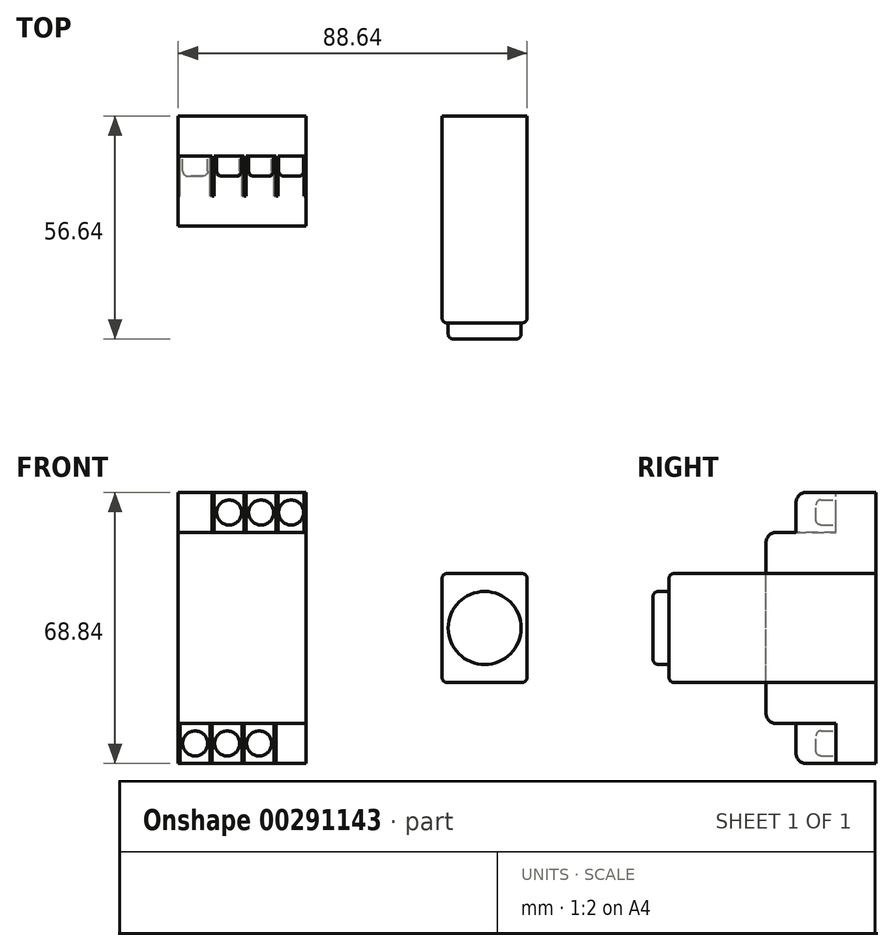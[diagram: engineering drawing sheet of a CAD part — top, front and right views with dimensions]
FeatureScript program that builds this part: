
annotation { "Feature Type Name" : "Feature", "Feature Type Description" : "" }
export const myFeature = defineFeature(function(context is Context, id is Id, definition is map)
    precondition{}
    {
        {
            var Q0;
            Q0=qCreatedBy(makeId("Front.planeOp"),FACE);
            var sketch = newSketch(context, id + "F0", { "sketchPlane" : qUnion([Q0])});
            skLineSegment(sketch, "E0.bottom", {"start": v(10.8, -13.84) * mm, "end": v(-10.8, -13.84) * mm});
            skLineSegment(sketch, "E0.top", {"start": v(10.8, 13.84) * mm, "end": v(-10.8, 13.84) * mm});
            skLineSegment(sketch, "E0.left", {"start": v(10.8, -13.84) * mm, "end": v(10.8, 13.84) * mm});
            skLineSegment(sketch, "E0.right", {"start": v(-10.8, -13.84) * mm, "end": v(-10.8, 13.84) * mm});
            skPoint(sketch, "E0.middle", {"position": v(0, 0) * mm});
            skSolve(sketch);
        }
        {
            var Q0;
            Q0 = qSketchRegion(id + "F0", true);
            extrude(context, id + "F1", {"entities" : qUnion([Q0]), "depth" : 52.58 * mm});
        }
        {
            var Q0;
            Q0=makeQuery(id+"F1.opExtrude","CAP_FACE",FACE,{"disambiguationData":[OSD([sQuery(id+"F0.wireOp",EDGE,"E0.bottom"),sQuery(id+"F0.wireOp",EDGE,"E0.top"),sQuery(id+"F0.wireOp",EDGE,"E0.left"),sQuery(id+"F0.wireOp",EDGE,"E0.right")])],"isStart":false});
            var sketch = newSketch(context, id + "F2", { "sketchPlane" : qUnion([Q0])});
            skCircle(sketch, "E1", {"center": v(0, 0) * mm, "radius": 9.27 * mm});
            skSolve(sketch);
        }
        {
            var Q0;
            Q0 = qSketchRegion(id + "F2", true);
            extrude(context, id + "F3", {"entities" : qUnion([Q0]), "operationType" : NewBodyOperationType.ADD, "depth" : 4.06 * mm});
        }
        {
            var Q0;
            Q0=makeQuery(id+"F3.opExtrude","CAP_EDGE",EDGE,{"disambiguationData":[OSD([sQuery(id+"F2.wireOp",EDGE,"E1")])],"isStart":false});
            fillet(context, id + "F4", {"entities" : qUnion([Q0]), "radius" : 1.27 * mm, "tangentPropagation" : true, "allowEdgeOverflow" : false});
        }
        {
            var Q0;
            Q0=makeQuery(id+"F1.opExtrude","CAP_EDGE",EDGE,{"disambiguationData":[OSD([sQuery(id+"F0.wireOp",EDGE,"E0.left")])],"isStart":false});
            var Q1;
            Q1=makeQuery(id+"F1.opExtrude","CAP_EDGE",EDGE,{"disambiguationData":[OSD([sQuery(id+"F0.wireOp",EDGE,"E0.bottom")])],"isStart":false});
            var Q2;
            Q2=makeQuery(id+"F1.opExtrude","CAP_EDGE",EDGE,{"disambiguationData":[OSD([sQuery(id+"F0.wireOp",EDGE,"E0.top")])],"isStart":false});
            var Q3;
            Q3=makeQuery(id+"F1.opExtrude","CAP_EDGE",EDGE,{"disambiguationData":[OSD([sQuery(id+"F0.wireOp",EDGE,"E0.right")])],"isStart":false});
            var Q4;
            Q4=makeQuery(id+"F1.opExtrude","SWEPT_EDGE",EDGE,{"disambiguationData":[OSD([sQuery(id+"F0.wireOp",EDGE,"E0.top"),sQuery(id+"F0.wireOp",EDGE,"E0.left")])]});
            var Q5;
            Q5=makeQuery(id+"F1.opExtrude","SWEPT_EDGE",EDGE,{"disambiguationData":[OSD([sQuery(id+"F0.wireOp",EDGE,"E0.bottom"),sQuery(id+"F0.wireOp",EDGE,"E0.left")])]});
            var Q6;
            Q6=makeQuery(id+"F1.opExtrude","SWEPT_EDGE",EDGE,{"disambiguationData":[OSD([sQuery(id+"F0.wireOp",EDGE,"E0.top"),sQuery(id+"F0.wireOp",EDGE,"E0.right")])]});
            var Q7;
            Q7=makeQuery(id+"F1.opExtrude","SWEPT_EDGE",EDGE,{"disambiguationData":[OSD([sQuery(id+"F0.wireOp",EDGE,"E0.bottom"),sQuery(id+"F0.wireOp",EDGE,"E0.right")])]});
            fillet(context, id + "F5", {"entities" : qUnion([Q0, Q1, Q2, Q3, Q4, Q5, Q6, Q7]), "radius" : 1.27 * mm, "tangentPropagation" : true, "allowEdgeOverflow" : false});
        }
        {
            var Q0;
            Q0=qCreatedBy(makeId("Front.planeOp"),FACE);
            var sketch = newSketch(context, id + "F6", { "sketchPlane" : qUnion([Q0])});
            skLineSegment(sketch, "E2.bottom", {"start": v(-77.85, -34.42) * mm, "end": v(-45.34, -34.42) * mm});
            skLineSegment(sketch, "E2.top", {"start": v(-77.85, 34.42) * mm, "end": v(-45.34, 34.42) * mm});
            skLineSegment(sketch, "E2.left", {"start": v(-77.85, -34.42) * mm, "end": v(-77.85, 34.42) * mm});
            skLineSegment(sketch, "E2.right", {"start": v(-45.34, -34.42) * mm, "end": v(-45.34, 34.42) * mm});
            skPoint(sketch, "E2.middle", {"position": v(-61.6, 0) * mm});
            skLineSegment(sketch, "E3.bottom", {"start": v(-77.85, 24.26) * mm, "end": v(-45.34, 24.26) * mm});
            skLineSegment(sketch, "E3.top", {"start": v(-77.85, -24.26) * mm, "end": v(-45.34, -24.26) * mm});
            skLineSegment(sketch, "E3.left", {"start": v(-77.85, 24.26) * mm, "end": v(-77.85, -24.26) * mm});
            skLineSegment(sketch, "E3.right", {"start": v(-45.34, 24.26) * mm, "end": v(-45.34, -24.26) * mm});
            skSolve(sketch);
        }
        {
            var Q0;
            Q0=makeQuery(id+"F6.imprint","IMPRINT",FACE,{"disambiguationData":[TD([[makeQuery(id+"F6.imprint","IMPRINT",EDGE,{"derivedFrom":sQuery(id+"F6.wireOp",EDGE,"E3.bottom")}),-1.0]])]});
            extrude(context, id + "F7", {"entities" : qUnion([Q0]), "depth" : 27.94 * mm});
        }
        {
            var Q0;
            {var subQ0=sQuery(id+"F6.wireOp",EDGE,"E2.top");Q0=makeQuery(id+"F6.imprint","IMPRINT",FACE,{"disambiguationData":[TD([[makeQuery(id+"F6.imprint","IMPRINT",EDGE,{"derivedFrom":subQ0}),-1.0]])]});}
            var Q1;
            {var subQ0=sQuery(id+"F6.wireOp",EDGE,"E2.bottom");Q1=makeQuery(id+"F6.imprint","IMPRINT",FACE,{"disambiguationData":[TD([[makeQuery(id+"F6.imprint","IMPRINT",EDGE,{"derivedFrom":subQ0}),1.0]])]});}
            extrude(context, id + "F8", {"entities" : qUnion([Q0, Q1]), "operationType" : NewBodyOperationType.ADD, "depth" : 10.16 * mm});
        }
        {
            var Q0;
            Q0=makeQuery(id+"F8.opExtrude","CAP_FACE",FACE,{"disambiguationData":[OSD([sQuery(id+"F6.wireOp",EDGE,"E2.top"),sQuery(id+"F6.wireOp",EDGE,"E2.left"),sQuery(id+"F6.wireOp",EDGE,"E2.right"),sQuery(id+"F6.wireOp",EDGE,"E3.bottom")])],"isStart":false});
            var sketch = newSketch(context, id + "F9", { "sketchPlane" : qUnion([Q0])});
            skLineSegment(sketch, "E4.bottom", {"start": v(-45.34, 34.42) * mm, "end": v(-69.22, 34.42) * mm});
            skLineSegment(sketch, "E4.top", {"start": v(-45.34, 24.26) * mm, "end": v(-69.22, 24.26) * mm});
            skLineSegment(sketch, "E4.left", {"start": v(-45.34, 34.42) * mm, "end": v(-45.34, 24.26) * mm});
            skLineSegment(sketch, "E4.right", {"start": v(-69.22, 34.42) * mm, "end": v(-69.22, 24.26) * mm});
            skSolve(sketch);
        }
        {
            var Q0;
            Q0 = qSketchRegion(id + "F9", true);
            extrude(context, id + "F10", {"entities" : qUnion([Q0]), "operationType" : NewBodyOperationType.ADD, "depth" : 10.16 * mm});
        }
        {
            var Q0;
            Q0=makeQuery(id+"F10.opExtrude","CAP_EDGE",EDGE,{"disambiguationData":[OSD([sQuery(id+"F9.wireOp",EDGE,"E4.bottom")])],"isStart":false});
            fillet(context, id + "F11", {"entities" : qUnion([Q0]), "radius" : 2.54 * mm, "tangentPropagation" : true, "allowEdgeOverflow" : false});
        }
        {
            var Q0;
            Q0=makeQuery(id+"F10.opExtrude","CAP_FACE",FACE,{"disambiguationData":[OSD([sQuery(id+"F9.wireOp",EDGE,"E4.bottom"),sQuery(id+"F9.wireOp",EDGE,"E4.top"),sQuery(id+"F9.wireOp",EDGE,"E4.left"),sQuery(id+"F9.wireOp",EDGE,"E4.right")])],"isStart":false});
            var sketch = newSketch(context, id + "F12", { "sketchPlane" : qUnion([Q0])});
            skPoint(sketch, "E5.centerSnap0", {"position": v(-45.34, 28.07) * mm});
            skPoint(sketch, "E5.centerSnap1", {"position": v(-57.28, 31.88) * mm});
            skPoint(sketch, "E6.centerSnap0", {"position": v(-69.22, 28.07) * mm});
            skLineSegment(sketch, "E7", {"start": v(-68.7, 24.26) * mm, "end": v(-68.7, 34.42) * mm});
            skLineSegment(sketch, "E8", {"start": v(-69.22, 34.42) * mm, "end": v(-69.22, 24.26) * mm});
            skLineSegment(sketch, "E9", {"start": v(-69.22, 24.26) * mm, "end": v(-68.7, 24.26) * mm});
            skLineSegment(sketch, "E10", {"start": v(-61.09, 34.42) * mm, "end": v(-61.09, 24.26) * mm});
            skLineSegment(sketch, "E11", {"start": v(-69.22, 24.26) * mm, "end": v(-45.34, 24.26) * mm});
            skLineSegment(sketch, "E12", {"start": v(-45.34, 24.26) * mm, "end": v(-45.34, 34.42) * mm});
            skLineSegment(sketch, "E13", {"start": v(-69.22, 34.42) * mm, "end": v(-45.34, 34.42) * mm});
            skLineSegment(sketch, "E14", {"start": v(-60.58, 34.42) * mm, "end": v(-60.58, 24.26) * mm});
            skLineSegment(sketch, "E15", {"start": v(-52.96, 34.42) * mm, "end": v(-52.96, 24.26) * mm});
            skLineSegment(sketch, "E16", {"start": v(-52.45, 34.42) * mm, "end": v(-52.45, 24.26) * mm});
            skLineSegment(sketch, "E17", {"start": v(-45.85, 34.42) * mm, "end": v(-45.85, 24.26) * mm});
            skSolve(sketch);
        }
        {
            var Q0;
            {var subQ0=sQuery(id+"F12.wireOp",EDGE,"E16");var subQ1=sQuery(id+"F12.wireOp",EDGE,"E11");var subQ2=makeQuery(id+"F12.imprint","INTERSECT",VERTEX,{"derivedFrom":[subQ1,subQ0]});Q0=makeQuery(id+"F12.imprint","IMPRINT",FACE,{"disambiguationData":[TD([[makeQuery(id+"F12.imprint","IMPRINT",EDGE,{"disambiguationData":[TD([[subQ2,-1.0]])],"derivedFrom":subQ1}),1.0]])]});}
            var Q1;
            {var subQ0=sQuery(id+"F12.wireOp",EDGE,"E16");var subQ1=sQuery(id+"F12.wireOp",EDGE,"E13");var subQ2=makeQuery(id+"F12.imprint","INTERSECT",VERTEX,{"derivedFrom":[subQ1,subQ0]});Q1=makeQuery(id+"F12.imprint","IMPRINT",FACE,{"disambiguationData":[TD([[makeQuery(id+"F12.imprint","IMPRINT",EDGE,{"disambiguationData":[TD([[subQ2,-1.0]])],"derivedFrom":subQ1}),-1.0]])]});}
            var Q2;
            {var subQ0=sQuery(id+"F12.wireOp",EDGE,"E14");var subQ1=sQuery(id+"F12.wireOp",EDGE,"E11");var subQ2=makeQuery(id+"F12.imprint","INTERSECT",VERTEX,{"derivedFrom":[subQ1,subQ0]});Q2=makeQuery(id+"F12.imprint","IMPRINT",FACE,{"disambiguationData":[TD([[makeQuery(id+"F12.imprint","IMPRINT",EDGE,{"disambiguationData":[TD([[subQ2,-1.0]])],"derivedFrom":subQ1}),1.0]])]});}
            var Q3;
            {var subQ0=sQuery(id+"F12.wireOp",EDGE,"E14");var subQ1=sQuery(id+"F12.wireOp",EDGE,"E13");var subQ2=makeQuery(id+"F12.imprint","INTERSECT",VERTEX,{"derivedFrom":[subQ1,subQ0]});Q3=makeQuery(id+"F12.imprint","IMPRINT",FACE,{"disambiguationData":[TD([[makeQuery(id+"F12.imprint","IMPRINT",EDGE,{"disambiguationData":[TD([[subQ2,-1.0]])],"derivedFrom":subQ1}),-1.0]])]});}
            var Q4;
            {var subQ0=sQuery(id+"F12.wireOp",EDGE,"E11");var subQ1=sQuery(id+"F12.wireOp",EDGE,"E7");var subQ2=makeQuery(id+"F12.imprint","INTERSECT",VERTEX,{"derivedFrom":[subQ1,subQ0]});Q4=makeQuery(id+"F12.imprint","IMPRINT",FACE,{"disambiguationData":[TD([[makeQuery(id+"F12.imprint","IMPRINT",EDGE,{"disambiguationData":[TD([[subQ2,-1.0]])],"derivedFrom":subQ0}),1.0]])]});}
            var Q5;
            {var subQ0=sQuery(id+"F12.wireOp",EDGE,"E13");var subQ1=sQuery(id+"F12.wireOp",EDGE,"E7");var subQ2=makeQuery(id+"F12.imprint","INTERSECT",VERTEX,{"derivedFrom":[subQ1,subQ0]});Q5=makeQuery(id+"F12.imprint","IMPRINT",FACE,{"disambiguationData":[TD([[makeQuery(id+"F12.imprint","IMPRINT",EDGE,{"disambiguationData":[TD([[subQ2,-1.0]])],"derivedFrom":subQ0}),-1.0]])]});}
            extrude(context, id + "F13", {"entities" : qUnion([Q0, Q1, Q2, Q3, Q4, Q5]), "operationType" : NewBodyOperationType.REMOVE, "oppositeDirection" : true, "depth" : 10.16 * mm});
        }
        {
            var Q0;
            Q0=makeQuery(id+"F13.boolean.opBoolean","COPY",FACE,{"derivedFrom":makeQuery(id+"F13.opExtrude","CAP_FACE",FACE,{"disambiguationData":[OSD([sQuery(id+"F12.wireOp",EDGE,"E7"),sQuery(id+"F12.wireOp",EDGE,"E10"),sQuery(id+"F12.wireOp",EDGE,"E11"),sQuery(id+"F12.wireOp",EDGE,"E13")])],"isStart":false})});
            var sketch = newSketch(context, id + "F14", { "sketchPlane" : qUnion([Q0])});
            skCircle(sketch, "E18", {"center": v(-64.9, 29.34) * mm, "radius": 3.18 * mm});
            skPoint(sketch, "E18.centerSnap0", {"position": v(-64.9, 34.42) * mm});
            skPoint(sketch, "E18.centerSnap1", {"position": v(-61.09, 29.34) * mm});
            skCircle(sketch, "E19", {"center": v(-56.77, 29.34) * mm, "radius": 3.18 * mm});
            skCircle(sketch, "E20", {"center": v(-49.15, 29.34) * mm, "radius": 3.18 * mm});
            skSolve(sketch);
        }
        {
            var Q0;
            Q0 = qSketchRegion(id + "F14", true);
            extrude(context, id + "F15", {"entities" : qUnion([Q0]), "operationType" : NewBodyOperationType.ADD, "depth" : 5.08 * mm});
        }
        {
            var Q0;
            Q0=makeQuery(id+"F15.opExtrude","CAP_EDGE",EDGE,{"disambiguationData":[OSD([sQuery(id+"F14.wireOp",EDGE,"E18")])],"isStart":false});
            var Q1;
            Q1=makeQuery(id+"F15.opExtrude","CAP_EDGE",EDGE,{"disambiguationData":[OSD([sQuery(id+"F14.wireOp",EDGE,"E19")])],"isStart":false});
            var Q2;
            Q2=makeQuery(id+"F15.opExtrude","CAP_EDGE",EDGE,{"disambiguationData":[OSD([sQuery(id+"F14.wireOp",EDGE,"E20")])],"isStart":false});
            fillet(context, id + "F16", {"entities" : qUnion([Q0, Q1, Q2]), "radius" : 1.27 * mm, "tangentPropagation" : true, "allowEdgeOverflow" : false});
        }
        {
            var Q0;
            Q0=makeQuery(id+"F8.opExtrude","CAP_FACE",FACE,{"disambiguationData":[OSD([sQuery(id+"F6.wireOp",EDGE,"E2.bottom"),sQuery(id+"F6.wireOp",EDGE,"E2.left"),sQuery(id+"F6.wireOp",EDGE,"E2.right"),sQuery(id+"F6.wireOp",EDGE,"E3.top")])],"isStart":false});
            var sketch = newSketch(context, id + "F17", { "sketchPlane" : qUnion([Q0])});
            skLineSegment(sketch, "E21", {"start": v(-77.85, -34.42) * mm, "end": v(-77.85, -24.26) * mm});
            skLineSegment(sketch, "E22", {"start": v(-77.85, -24.26) * mm, "end": v(-77.34, -24.26) * mm});
            skLineSegment(sketch, "E23", {"start": v(-77.34, -24.26) * mm, "end": v(-77.34, -34.42) * mm});
            skLineSegment(sketch, "E24.1.0.0", {"start": v(-69.22, -24.26) * mm, "end": v(-69.22, -34.42) * mm});
            skLineSegment(sketch, "E24.1.0.1", {"start": v(-69.72, -34.42) * mm, "end": v(-69.72, -24.26) * mm});
            skLineSegment(sketch, "E24.2.0.0", {"start": v(-61.09, -24.26) * mm, "end": v(-61.09, -34.42) * mm});
            skLineSegment(sketch, "E24.2.0.1", {"start": v(-61.6, -34.42) * mm, "end": v(-61.6, -24.26) * mm});
            skLineSegment(sketch, "E24.3.0.0", {"start": v(-52.96, -24.26) * mm, "end": v(-52.96, -34.42) * mm});
            skLineSegment(sketch, "E24.3.0.1", {"start": v(-53.47, -34.42) * mm, "end": v(-53.47, -24.26) * mm});
            skLineSegment(sketch, "E24.4.0.0", {"start": v(-44.83, -24.26) * mm, "end": v(-44.83, -34.42) * mm});
            skLineSegment(sketch, "E24.4.0.1", {"start": v(-45.34, -34.42) * mm, "end": v(-45.34, -24.26) * mm});
            skLineSegment(sketch, "E24.direction1", {"start": v(-77.34, -34.42) * mm, "end": v(-69.22, -34.42) * mm, "construction": true});
            skLineSegment(sketch, "E25", {"start": v(-77.34, -24.26) * mm, "end": v(-77.85, -24.26) * mm});
            skLineSegment(sketch, "E26", {"start": v(-77.34, -34.42) * mm, "end": v(-77.85, -34.42) * mm});
            skLineSegment(sketch, "E27", {"start": v(-69.72, -34.42) * mm, "end": v(-69.22, -34.42) * mm});
            skLineSegment(sketch, "E28", {"start": v(-69.72, -24.26) * mm, "end": v(-69.22, -24.26) * mm});
            skLineSegment(sketch, "E29", {"start": v(-61.6, -24.26) * mm, "end": v(-61.09, -24.26) * mm});
            skLineSegment(sketch, "E30", {"start": v(-61.09, -34.42) * mm, "end": v(-61.6, -34.42) * mm});
            skLineSegment(sketch, "E31", {"start": v(-53.47, -24.26) * mm, "end": v(-52.96, -24.26) * mm});
            skLineSegment(sketch, "E32", {"start": v(-53.47, -34.42) * mm, "end": v(-52.96, -34.42) * mm});
            skSolve(sketch);
        }
        {
            var Q0;
            Q0 = qSketchRegion(id + "F17", true);
            extrude(context, id + "F18", {"entities" : qUnion([Q0]), "operationType" : NewBodyOperationType.ADD, "depth" : 10.16 * mm});
        }
        {
            var Q0;
            Q0=makeQuery(id+"F18.opExtrude","CAP_EDGE",EDGE,{"disambiguationData":[OSD([sQuery(id+"F17.wireOp",EDGE,"E26")])],"isStart":false});
            var Q1;
            Q1=makeQuery(id+"F18.opExtrude","CAP_EDGE",EDGE,{"disambiguationData":[OSD([sQuery(id+"F17.wireOp",EDGE,"E27")])],"isStart":false});
            var Q2;
            Q2=makeQuery(id+"F18.opExtrude","CAP_EDGE",EDGE,{"disambiguationData":[OSD([sQuery(id+"F17.wireOp",EDGE,"E30")])],"isStart":false});
            var Q3;
            Q3=makeQuery(id+"F18.opExtrude","CAP_EDGE",EDGE,{"disambiguationData":[OSD([sQuery(id+"F17.wireOp",EDGE,"E32")])],"isStart":false});
            fillet(context, id + "F19", {"entities" : qUnion([Q0, Q1, Q2, Q3]), "radius" : 2.54 * mm, "tangentPropagation" : true, "allowEdgeOverflow" : false});
        }
        {
            var Q0;
            {var subQ0=sQuery(id+"F6.wireOp",EDGE,"E2.bottom");var subQ1=sQuery(id+"F6.wireOp",EDGE,"E3.top");Q0=makeQuery(id+"F18.boolean.opBoolean","SPLIT",FACE,{"disambiguationData":[TD([makeQuery(id+"F18.opExtrude","SWEPT_FACE",FACE,{"disambiguationData":[OSD([sQuery(id+"F17.wireOp",EDGE,"E23")])]})])],"derivedFrom":makeQuery(id+"F8.opExtrude","CAP_FACE",FACE,{"disambiguationData":[OSD([subQ0,sQuery(id+"F6.wireOp",EDGE,"E2.left"),sQuery(id+"F6.wireOp",EDGE,"E2.right"),subQ1])],"isStart":false})});}
            var sketch = newSketch(context, id + "F20", { "sketchPlane" : qUnion([Q0])});
            skCircle(sketch, "E33", {"center": v(-73.53, -29.34) * mm, "radius": 3.18 * mm});
            skPoint(sketch, "E33.centerSnap0", {"position": v(-69.72, -29.34) * mm});
            skPoint(sketch, "E33.centerSnap1", {"position": v(-73.53, -34.42) * mm});
            skCircle(sketch, "E34", {"center": v(-65.4, -29.34) * mm, "radius": 3.18 * mm});
            skCircle(sketch, "E35", {"center": v(-57.28, -29.34) * mm, "radius": 3.18 * mm});
            skSolve(sketch);
        }
        {
            var Q0;
            Q0 = qSketchRegion(id + "F20", true);
            extrude(context, id + "F21", {"entities" : qUnion([Q0]), "operationType" : NewBodyOperationType.ADD, "depth" : 5.08 * mm});
        }
        {
            var Q0;
            Q0=makeQuery(id+"F21.opExtrude","CAP_EDGE",EDGE,{"disambiguationData":[OSD([sQuery(id+"F20.wireOp",EDGE,"E33")])],"isStart":false});
            var Q1;
            Q1=makeQuery(id+"F21.opExtrude","CAP_EDGE",EDGE,{"disambiguationData":[OSD([sQuery(id+"F20.wireOp",EDGE,"E34")])],"isStart":false});
            var Q2;
            Q2=makeQuery(id+"F21.opExtrude","CAP_EDGE",EDGE,{"disambiguationData":[OSD([sQuery(id+"F20.wireOp",EDGE,"E35")])],"isStart":false});
            fillet(context, id + "F22", {"entities" : qUnion([Q0, Q1, Q2]), "radius" : 1.27 * mm, "tangentPropagation" : true, "allowEdgeOverflow" : false});
        }
        {
            var Q0;
            Q0=makeQuery(id+"F7.opExtrude","CAP_EDGE",EDGE,{"disambiguationData":[OSD([sQuery(id+"F6.wireOp",EDGE,"E3.top")])],"isStart":false});
            var Q1;
            Q1=makeQuery(id+"F7.opExtrude","CAP_EDGE",EDGE,{"disambiguationData":[OSD([sQuery(id+"F6.wireOp",EDGE,"E3.bottom")])],"isStart":false});
            fillet(context, id + "F23", {"entities" : qUnion([Q0, Q1]), "radius" : 2.54 * mm, "tangentPropagation" : true, "allowEdgeOverflow" : false});
        }
    });
